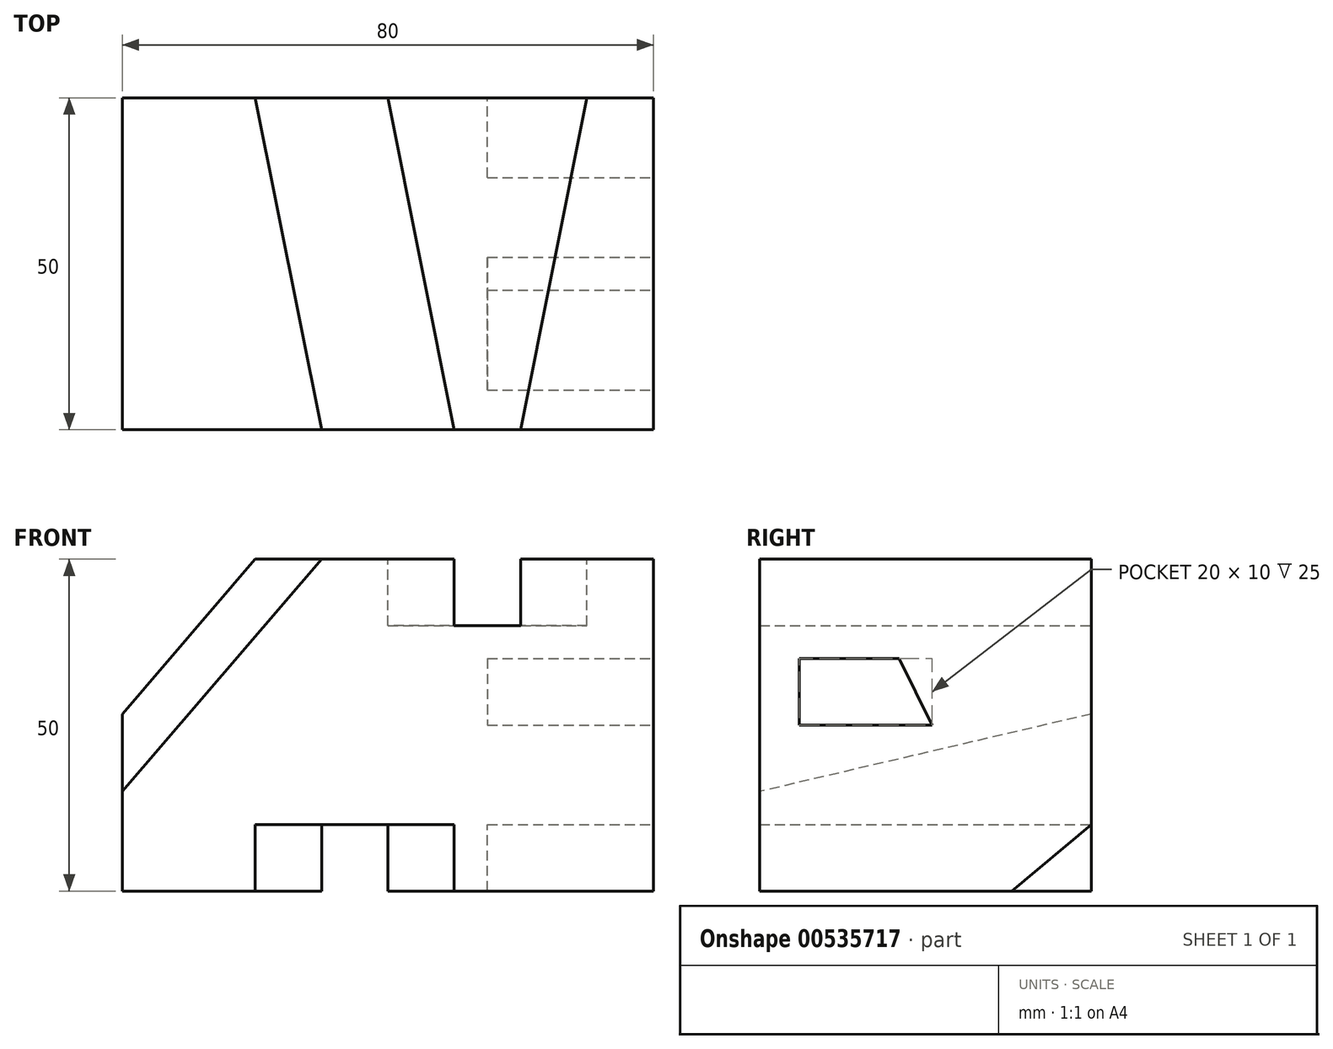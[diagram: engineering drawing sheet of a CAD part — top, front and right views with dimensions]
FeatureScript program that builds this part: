
annotation { "Feature Type Name" : "Feature", "Feature Type Description" : "" }
export const myFeature = defineFeature(function(context is Context, id is Id, definition is map)
    precondition{}
    {
        {
            var Q0;
            Q0=qCreatedBy(makeId("Front.planeOp"),FACE);
            var sketch = newSketch(context, id + "F0", { "sketchPlane" : qUnion([Q0])});
            skLineSegment(sketch, "E0.bottom", {"start": v(0, 0) * mm, "end": v(-80, 0) * mm});
            skLineSegment(sketch, "E0.top", {"start": v(0, 50) * mm, "end": v(-80, 50) * mm});
            skLineSegment(sketch, "E0.left", {"start": v(0, 0) * mm, "end": v(0, 50) * mm});
            skLineSegment(sketch, "E0.right", {"start": v(-80, 0) * mm, "end": v(-80, 50) * mm});
            skSolve(sketch);
        }
        {
            var Q0;
            Q0=makeQuery(id+"F0.imprint","IMPRINT",FACE,{"disambiguationData":[TD([[makeQuery(id+"F0.imprint","IMPRINT",EDGE,{"derivedFrom":sQuery(id+"F0.wireOp",EDGE,"E0.bottom")}),-1.0]])]});
            extrude(context, id + "F1", {"entities" : qUnion([Q0]), "depth" : 50 * mm, "offsetDistance" : 25 * mm});
        }
        {
            var Q0;
            Q0=makeQuery(id+"F1.opExtrude","SWEPT_FACE",FACE,{"disambiguationData":[OSD([sQuery(id+"F0.wireOp",EDGE,"E0.bottom")])]});
            var sketch = newSketch(context, id + "F2", { "sketchPlane" : qUnion([Q0])});
            skLineSegment(sketch, "E1", {"start": v(-60, 50) * mm, "end": v(-30, 50) * mm});
            skLineSegment(sketch, "E2", {"start": v(-30, 50) * mm, "end": v(-40, 0) * mm});
            skLineSegment(sketch, "E3", {"start": v(-40, 0) * mm, "end": v(-50, 0) * mm});
            skLineSegment(sketch, "E4", {"start": v(-50, 0) * mm, "end": v(-60, 50) * mm});
            skSolve(sketch);
        }
        {
            var Q0;
            Q0=makeQuery(id+"F2.imprint","IMPRINT",FACE,{"disambiguationData":[TD([[makeQuery(id+"F2.imprint","IMPRINT",EDGE,{"derivedFrom":sQuery(id+"F2.wireOp",EDGE,"E1")}),1.0]])]});
            extrude(context, id + "F3", {"entities" : qUnion([Q0]), "operationType" : NewBodyOperationType.REMOVE, "oppositeDirection" : true, "depth" : 10 * mm, "offsetDistance" : 25 * mm});
        }
        {
            var Q0;
            Q0=makeQuery(id+"F1.opExtrude","SWEPT_FACE",FACE,{"disambiguationData":[OSD([sQuery(id+"F0.wireOp",EDGE,"E0.top")])]});
            var sketch = newSketch(context, id + "F4", { "sketchPlane" : qUnion([Q0])});
            skLineSegment(sketch, "E5", {"start": v(-30, -50) * mm, "end": v(-20, -50) * mm});
            skLineSegment(sketch, "E6", {"start": v(-20, -50) * mm, "end": v(-10, 0) * mm});
            skLineSegment(sketch, "E7", {"start": v(-10, 0) * mm, "end": v(-40, 0) * mm});
            skLineSegment(sketch, "E8", {"start": v(-40, 0) * mm, "end": v(-30, -50) * mm});
            skSolve(sketch);
        }
        {
            var Q0;
            Q0=makeQuery(id+"F4.imprint","IMPRINT",FACE,{"disambiguationData":[TD([[makeQuery(id+"F4.imprint","IMPRINT",EDGE,{"derivedFrom":sQuery(id+"F4.wireOp",EDGE,"E5")}),-1.0]])]});
            extrude(context, id + "F5", {"entities" : qUnion([Q0]), "operationType" : NewBodyOperationType.REMOVE, "oppositeDirection" : true, "depth" : 10 * mm, "offsetDistance" : 25 * mm});
        }
        {
            var Q0;
            Q0=makeQuery(id+"F1.opExtrude","SWEPT_FACE",FACE,{"disambiguationData":[OSD([sQuery(id+"F0.wireOp",EDGE,"E0.left")])]});
            var sketch = newSketch(context, id + "F6", { "sketchPlane" : qUnion([Q0])});
            skLineSegment(sketch, "E9", {"start": v(-44, 35) * mm, "end": v(-44, 25) * mm});
            skLineSegment(sketch, "E10", {"start": v(-44, 25) * mm, "end": v(-24, 25) * mm});
            skLineSegment(sketch, "E11", {"start": v(-24, 25) * mm, "end": v(-29, 35) * mm});
            skLineSegment(sketch, "E12", {"start": v(-29, 35) * mm, "end": v(-44, 35) * mm});
            skSolve(sketch);
        }
        {
            var Q0;
            Q0=makeQuery(id+"F6.imprint","IMPRINT",FACE,{"disambiguationData":[TD([[makeQuery(id+"F6.imprint","IMPRINT",EDGE,{"derivedFrom":sQuery(id+"F6.wireOp",EDGE,"E9")}),1.0]])]});
            extrude(context, id + "F7", {"entities" : qUnion([Q0]), "operationType" : NewBodyOperationType.REMOVE, "oppositeDirection" : true, "depth" : 25 * mm, "offsetDistance" : 25 * mm});
        }
        {
            var Q0;
            Q0=makeQuery(id+"F1.opExtrude","SWEPT_FACE",FACE,{"disambiguationData":[OSD([sQuery(id+"F0.wireOp",EDGE,"E0.left")])]});
            var sketch = newSketch(context, id + "F8", { "sketchPlane" : qUnion([Q0])});
            skLineSegment(sketch, "E13", {"start": v(-12, 0) * mm, "end": v(0, 0) * mm});
            skLineSegment(sketch, "E14", {"start": v(0, 0) * mm, "end": v(0, 10) * mm});
            skLineSegment(sketch, "E15", {"start": v(0, 10) * mm, "end": v(-12, 0) * mm});
            skSolve(sketch);
        }
        {
            var Q0;
            Q0=makeQuery(id+"F8.imprint","IMPRINT",FACE,{"disambiguationData":[TD([[makeQuery(id+"F8.imprint","IMPRINT",EDGE,{"derivedFrom":sQuery(id+"F8.wireOp",EDGE,"E13")}),1.0]])]});
            extrude(context, id + "F9", {"entities" : qUnion([Q0]), "operationType" : NewBodyOperationType.REMOVE, "oppositeDirection" : true, "depth" : 25 * mm, "offsetDistance" : 25 * mm});
        }
        {
            var Q0;
            Q0=makeQuery(id+"F1.opExtrude","CAP_FACE",FACE,{"disambiguationData":[OSD([sQuery(id+"F0.wireOp",EDGE,"E0.bottom"),sQuery(id+"F0.wireOp",EDGE,"E0.top"),sQuery(id+"F0.wireOp",EDGE,"E0.left"),sQuery(id+"F0.wireOp",EDGE,"E0.right")])],"isStart":false});
            var sketch = newSketch(context, id + "F10", { "sketchPlane" : qUnion([Q0])});
            skLineSegment(sketch, "E16", {"start": v(-80, 50) * mm, "end": v(-80, 15) * mm});
            skLineSegment(sketch, "E17", {"start": v(-80, 15) * mm, "end": v(-50, 50) * mm});
            skLineSegment(sketch, "E18", {"start": v(-50, 50) * mm, "end": v(-80, 50) * mm});
            skSolve(sketch);
        }
        {
            var Q0;
            Q0=makeQuery(id+"F1.opExtrude","CAP_FACE",FACE,{"disambiguationData":[OSD([sQuery(id+"F0.wireOp",EDGE,"E0.bottom"),sQuery(id+"F0.wireOp",EDGE,"E0.top"),sQuery(id+"F0.wireOp",EDGE,"E0.left"),sQuery(id+"F0.wireOp",EDGE,"E0.right")])],"isStart":true});
            var sketch = newSketch(context, id + "F11", { "sketchPlane" : qUnion([Q0])});
            skLineSegment(sketch, "E19", {"start": v(80, 50) * mm, "end": v(60, 50) * mm});
            skLineSegment(sketch, "E20", {"start": v(60, 50) * mm, "end": v(80, 25) * mm});
            skSolve(sketch);
        }
        {
            var Q0;
            {var subQ0=sQuery(id+"F0.wireOp",EDGE,"E0.right");var subQ2=sQuery(id+"F0.wireOp",EDGE,"E0.top");Q0=makeQuery(id+"F5.boolean.opBoolean","SPLIT",FACE,{"disambiguationData":[TD([makeQuery(id+"F1.opExtrude","SWEPT_FACE",FACE,{"disambiguationData":[OSD([subQ0])]})])],"derivedFrom":makeQuery(id+"F1.opExtrude","SWEPT_FACE",FACE,{"disambiguationData":[OSD([subQ2])]})});}
            var sketch = newSketch(context, id + "F12", { "sketchPlane" : qUnion([Q0])});
            skLineSegment(sketch, "E21", {"start": v(-60, 0) * mm, "end": v(-50, -50) * mm});
            skSolve(sketch);
        }
        {
            var Q0;
            Q0=makeQuery(id+"F10.imprint","IMPRINT",FACE,{"disambiguationData":[TD([[makeQuery(id+"F10.imprint","IMPRINT",EDGE,{"derivedFrom":sQuery(id+"F10.wireOp",EDGE,"E16")}),-1.0]])]});
            var Q1;
            Q1=sQuery(id+"F12.wireOp",EDGE,"E21");
            sweep(context, id + "F13", {"operationType" : NewBodyOperationType.REMOVE, "profiles" : qUnion([Q0]), "path" : qUnion([Q1])});
        }
    });
